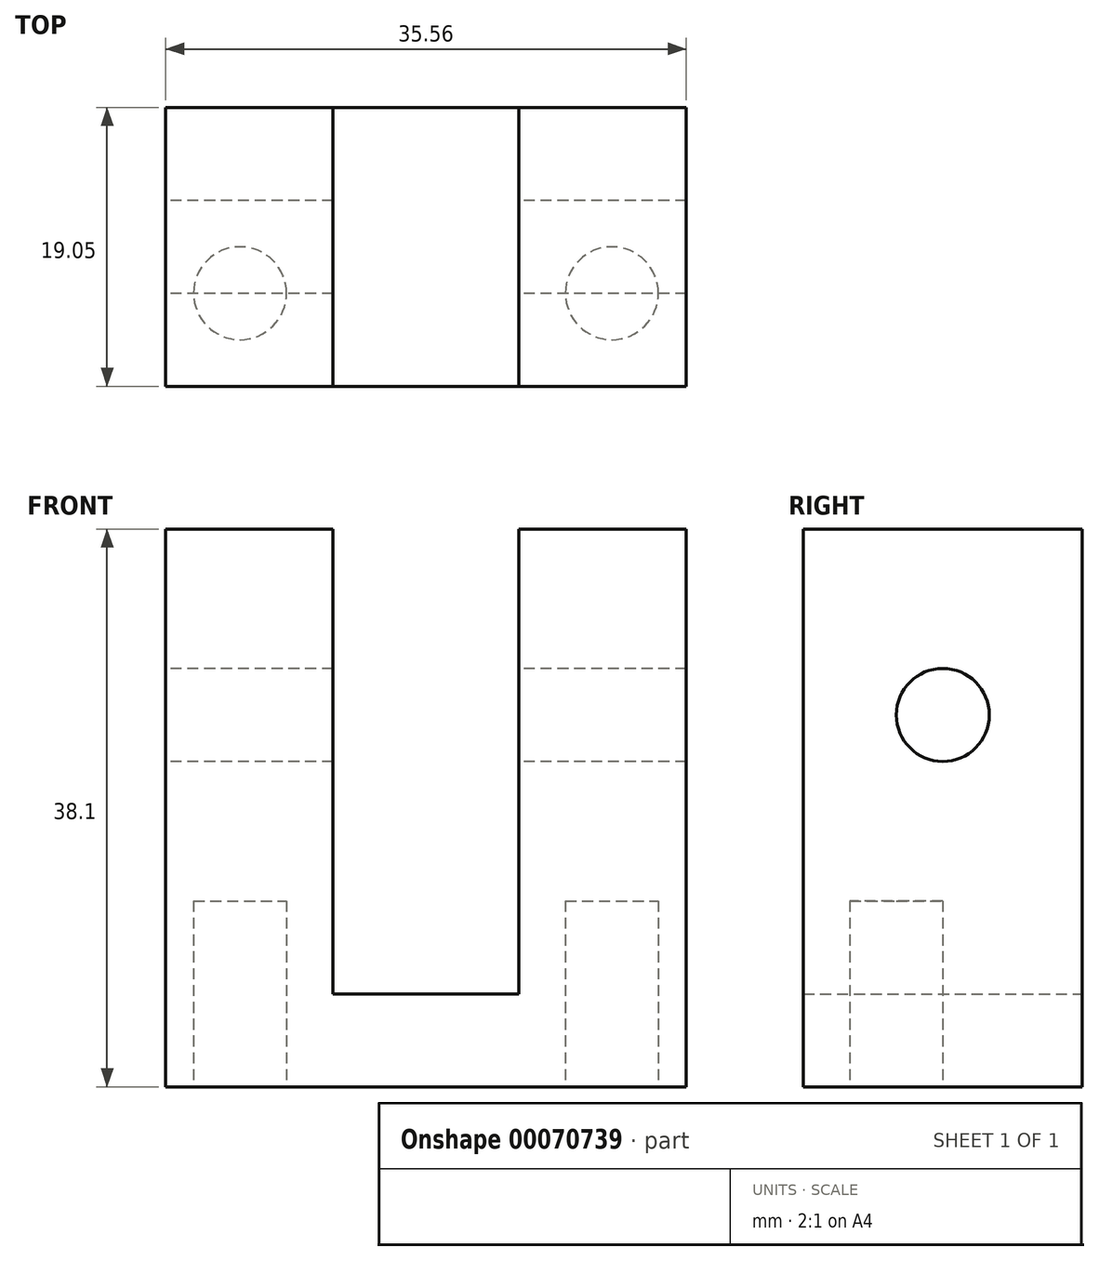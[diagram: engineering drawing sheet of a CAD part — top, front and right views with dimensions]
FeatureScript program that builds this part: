
annotation { "Feature Type Name" : "Feature", "Feature Type Description" : "" }
export const myFeature = defineFeature(function(context is Context, id is Id, definition is map)
    precondition{}
    {
        {
            var Q0;
            Q0=qCreatedBy(makeId("Front.planeOp"),FACE);
            var sketch = newSketch(context, id + "F0", { "sketchPlane" : qUnion([Q0])});
            skLineSegment(sketch, "E0.bottom", {"start": v(0, 0) * mm, "end": v(35.56, 0) * mm});
            skLineSegment(sketch, "E0.top", {"start": v(0, 38.1) * mm, "end": v(11.43, 38.1) * mm});
            skLineSegment(sketch, "E0.left", {"start": v(0, 0) * mm, "end": v(0, 38.1) * mm});
            skLineSegment(sketch, "E0.right", {"start": v(35.56, 0) * mm, "end": v(35.56, 38.1) * mm});
            skLineSegment(sketch, "E1.top", {"start": v(11.43, 6.35) * mm, "end": v(24.13, 6.35) * mm});
            skLineSegment(sketch, "E1.left", {"start": v(11.43, 38.1) * mm, "end": v(11.43, 6.35) * mm});
            skLineSegment(sketch, "E1.right", {"start": v(24.13, 38.1) * mm, "end": v(24.13, 6.35) * mm});
            skLineSegment(sketch, "E2.trimOffspring", {"start": v(24.13, 38.1) * mm, "end": v(35.56, 38.1) * mm});
            skSolve(sketch);
        }
        {
            var Q0;
            Q0 = qSketchRegion(id + "F0", true);
            extrude(context, id + "F1", {"entities" : qUnion([Q0]), "depth" : 19.05 * mm});
        }
        {
            var Q0;
            Q0=makeQuery(id+"F1.opExtrude","SWEPT_FACE",FACE,{"disambiguationData":[OSD([sQuery(id+"F0.wireOp",EDGE,"E0.bottom")])]});
            var sketch = newSketch(context, id + "F2", { "sketchPlane" : qUnion([Q0])});
            skCircle(sketch, "E3", {"center": v(5.08, 12.7) * mm, "radius": 3.18 * mm});
            skCircle(sketch, "E4", {"center": v(30.48, 12.7) * mm, "radius": 3.18 * mm});
            skSolve(sketch);
        }
        {
            var Q0;
            Q0=makeQuery(id+"F2.imprint","IMPRINT",FACE,{"disambiguationData":[TD([[makeQuery(id+"F2.imprint","IMPRINT",EDGE,{"derivedFrom":sQuery(id+"F2.wireOp",EDGE,"E3")}),1.0]])]});
            var Q1;
            Q1=makeQuery(id+"F2.imprint","IMPRINT",FACE,{"disambiguationData":[TD([[makeQuery(id+"F2.imprint","IMPRINT",EDGE,{"derivedFrom":sQuery(id+"F2.wireOp",EDGE,"E4")}),1.0]])]});
            extrude(context, id + "F3", {"entities" : qUnion([Q0, Q1]), "operationType" : NewBodyOperationType.REMOVE, "oppositeDirection" : true, "depth" : 12.7 * mm});
        }
        {
            var Q0;
            Q0=makeQuery(id+"F1.opExtrude","SWEPT_FACE",FACE,{"disambiguationData":[OSD([sQuery(id+"F0.wireOp",EDGE,"E0.left")])]});
            var sketch = newSketch(context, id + "F4", { "sketchPlane" : qUnion([Q0])});
            skCircle(sketch, "E5", {"center": v(9.53, 25.4) * mm, "radius": 3.18 * mm});
            skPoint(sketch, "E5.centerSnap0", {"position": v(9.53, 38.1) * mm});
            skSolve(sketch);
        }
        {
            var Q0;
            Q0 = qSketchRegion(id + "F4", true);
            extrude(context, id + "F5", {"entities" : qUnion([Q0]), "operationType" : NewBodyOperationType.REMOVE, "oppositeDirection" : true, "depth" : 254 * mm});
        }
    });
